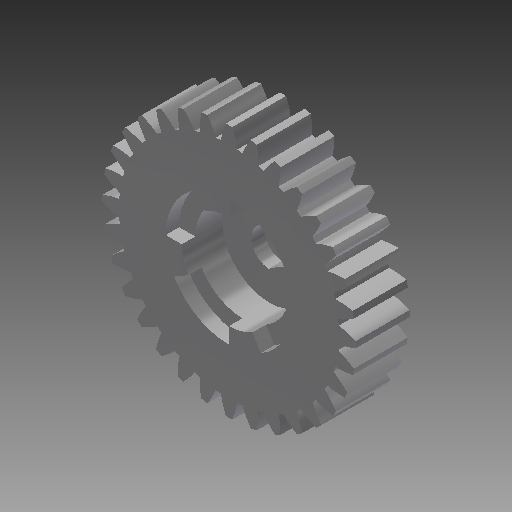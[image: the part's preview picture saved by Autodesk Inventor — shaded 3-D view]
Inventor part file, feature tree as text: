
AUTODESK INVENTOR PART (.ipt)
format: ipt  version: 2017 (Build 210142000, 142)  size: 309,760 bytes
history: native  units: mm (DEFAULTED — no unit token found)
features: sketch x5, extrude x4, plane x3, other x3, pattern_circular x1
ambient origin geometry x8: Origin, YZ Plane, XZ Plane, XY Plane, X Axis, Y Axis, Z Axis, Center Point
bodies: Solid1 (feature_tree)
feature tree (16):
  extrude  "Extrusion1"  Depth=20.0mm TaperAngle=0.0deg
  plane  "Work Plane2"
  plane  "Work Plane8"
  plane  "Work Plane9"
  other  "Spur Gear"
  extrude  "Extrusion2"  Depth=10.0mm TaperAngle=0.0deg
  extrude  "Extrusion3"  Depth=0.981748mm TaperAngle=0.0deg
  extrude  "Extrusion4"  TaperAngle=0.0deg  [1 undecoded]
  pattern_circular  "Circular Pattern1"  Count=8  [1 undecoded]
  sketch  "Sketch1"  dims[d0=94.0mm d1=20.0mm d2=0.0mm]
  sketch  "Sketch2"  dims[d3=88.275862mm d4=10.0mm d5=0.0mm]
  other  "Srf1"
  sketch  "Sketch3"  dims[d16=80.0mm d17=0.0mm d34=0.981748mm]
  sketch  "Sketch4"  dims[d39=0.0mm d41=0.0mm d43=80.0mm]
  sketch  "Sketch5"  dims[d46=80.0mm d47=0.0mm d48=0.0mm d49=13.5mm d50=10.0mm d51=0.0mm d52=35.0mm d53=15.0mm d54=0.0mm d55=60.0deg d56=6.0mm d57=5.0mm d58=0.0mm d59=40.0mm d60=360.0deg]
  other  "Pitch Diameter"
note: 2 required parameter values undecoded (feature->parameter linkage not recoverable at this tier; creation-order binding heuristic only, values carry confidence <= 0.55)
